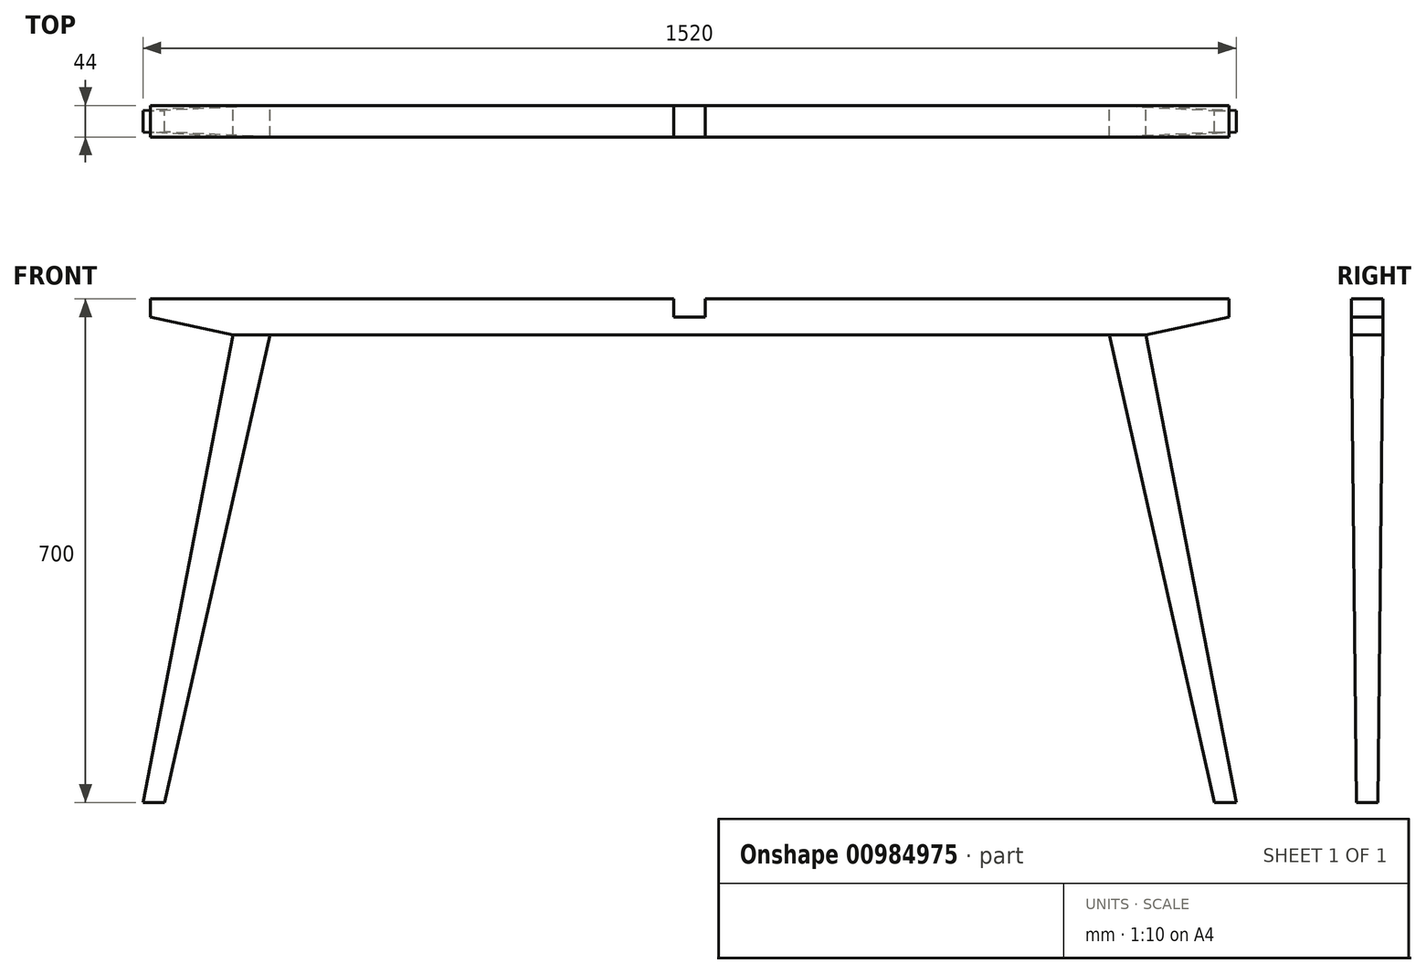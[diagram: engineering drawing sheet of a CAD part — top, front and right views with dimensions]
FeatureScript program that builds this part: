
annotation { "Feature Type Name" : "Feature", "Feature Type Description" : "" }
export const myFeature = defineFeature(function(context is Context, id is Id, definition is map)
    precondition{}
    {
        {
            var Q0;
            Q0=qCreatedBy(makeId("Front.planeOp"),FACE);
            var sketch = newSketch(context, id + "F0", { "sketchPlane" : qUnion([Q0])});
            skLineSegment(sketch, "E0", {"start": v(0, 0) * mm, "end": v(0, -700) * mm, "construction": true});
            skLineSegment(sketch, "E1", {"start": v(0, -700) * mm, "end": v(-80.07, -700) * mm, "construction": true});
            skLineSegment(sketch, "E2", {"start": v(-22, 0) * mm, "end": v(-750, 0) * mm});
            skLineSegment(sketch, "E3", {"start": v(-750, 0) * mm, "end": v(-625, 0) * mm, "construction": true});
            skLineSegment(sketch, "E4", {"start": v(-750, 0) * mm, "end": v(-750, -25) * mm});
            skLineSegment(sketch, "E5", {"start": v(-760, -700) * mm, "end": v(-634.64, -50) * mm});
            skLineSegment(sketch, "E6.0", {"start": v(0, -50) * mm, "end": v(-583.72, -50) * mm});
            skLineSegment(sketch, "E7", {"start": v(-750, 0) * mm, "end": v(-750, -25) * mm, "construction": true});
            skLineSegment(sketch, "E8", {"start": v(-750, -25) * mm, "end": v(-634.64, -50) * mm});
            skLineSegment(sketch, "E9", {"start": v(-760, -700) * mm, "end": v(-730, -700) * mm});
            skLineSegment(sketch, "E10", {"start": v(-730, -700) * mm, "end": v(-583.72, -50) * mm});
            skLineSegment(sketch, "E11.MirrorCS", {"start": v(22, 0) * mm, "end": v(750, 0) * mm});
            skLineSegment(sketch, "E12.MirrorCS", {"start": v(750, 0) * mm, "end": v(750, -25) * mm});
            skLineSegment(sketch, "E13.MirrorCS", {"start": v(750, -25) * mm, "end": v(634.64, -50) * mm});
            skLineSegment(sketch, "E14.MirrorCS", {"start": v(760, -700) * mm, "end": v(634.64, -50) * mm});
            skLineSegment(sketch, "E15.MirrorCS", {"start": v(730, -700) * mm, "end": v(583.72, -50) * mm});
            skLineSegment(sketch, "E16.MirrorCS", {"start": v(0, -50) * mm, "end": v(583.72, -50) * mm});
            skLineSegment(sketch, "E17.MirrorCS", {"start": v(760, -700) * mm, "end": v(730, -700) * mm});
            skLineSegment(sketch, "E18", {"start": v(-22, 0) * mm, "end": v(-22, -25) * mm});
            skLineSegment(sketch, "E19", {"start": v(-22, -25) * mm, "end": v(0, -25) * mm});
            skLineSegment(sketch, "E20.MirrorCS", {"start": v(22, 0) * mm, "end": v(22, -25) * mm});
            skLineSegment(sketch, "E21.MirrorCS", {"start": v(22, -25) * mm, "end": v(0, -25) * mm});
            skPoint(sketch, "E22.orphan", {"position": v(0, 0) * mm});
            skSolve(sketch);
        }
        {
            var Q0;
            Q0 = qSketchRegion(id + "F0", true);
            extrude(context, id + "F1", {"entities" : qUnion([Q0]), "depth" : 44 * mm, "offsetDistance" : 25 * mm});
        }
        {
            var Q0;
            Q0=qCreatedBy(makeId("Right.planeOp"),FACE);
            var sketch = newSketch(context, id + "F2", { "sketchPlane" : qUnion([Q0])});
            skLineSegment(sketch, "E23", {"start": v(0, 0) * mm, "end": v(0, -50) * mm, "construction": true});
            skLineSegment(sketch, "E24", {"start": v(0, -50) * mm, "end": v(0, -700) * mm});
            skLineSegment(sketch, "E25", {"start": v(-22, -700) * mm, "end": v(-22, -631.39) * mm, "construction": true});
            skLineSegment(sketch, "E26", {"start": v(0, -700) * mm, "end": v(-7, -700) * mm});
            skLineSegment(sketch, "E27", {"start": v(-7, -700) * mm, "end": v(0, -50) * mm});
            skLineSegment(sketch, "E28.MirrorCS", {"start": v(-37, -700) * mm, "end": v(-44, -50) * mm});
            skLineSegment(sketch, "E29.MirrorCS", {"start": v(-44, -50) * mm, "end": v(-44, -700) * mm});
            skLineSegment(sketch, "E30.MirrorCS", {"start": v(-44, -700) * mm, "end": v(-37, -700) * mm});
            skSolve(sketch);
        }
        {
            var Q0;
            Q0 = qSketchRegion(id + "F2", true);
            extrude(context, id + "F3", {"entities" : qUnion([Q0]), "operationType" : NewBodyOperationType.REMOVE, "endBound" : BoundingType.SYMMETRIC, "oppositeDirection" : true, "depth" : 1808 * mm, "offsetDistance" : 25 * mm});
        }
    });
